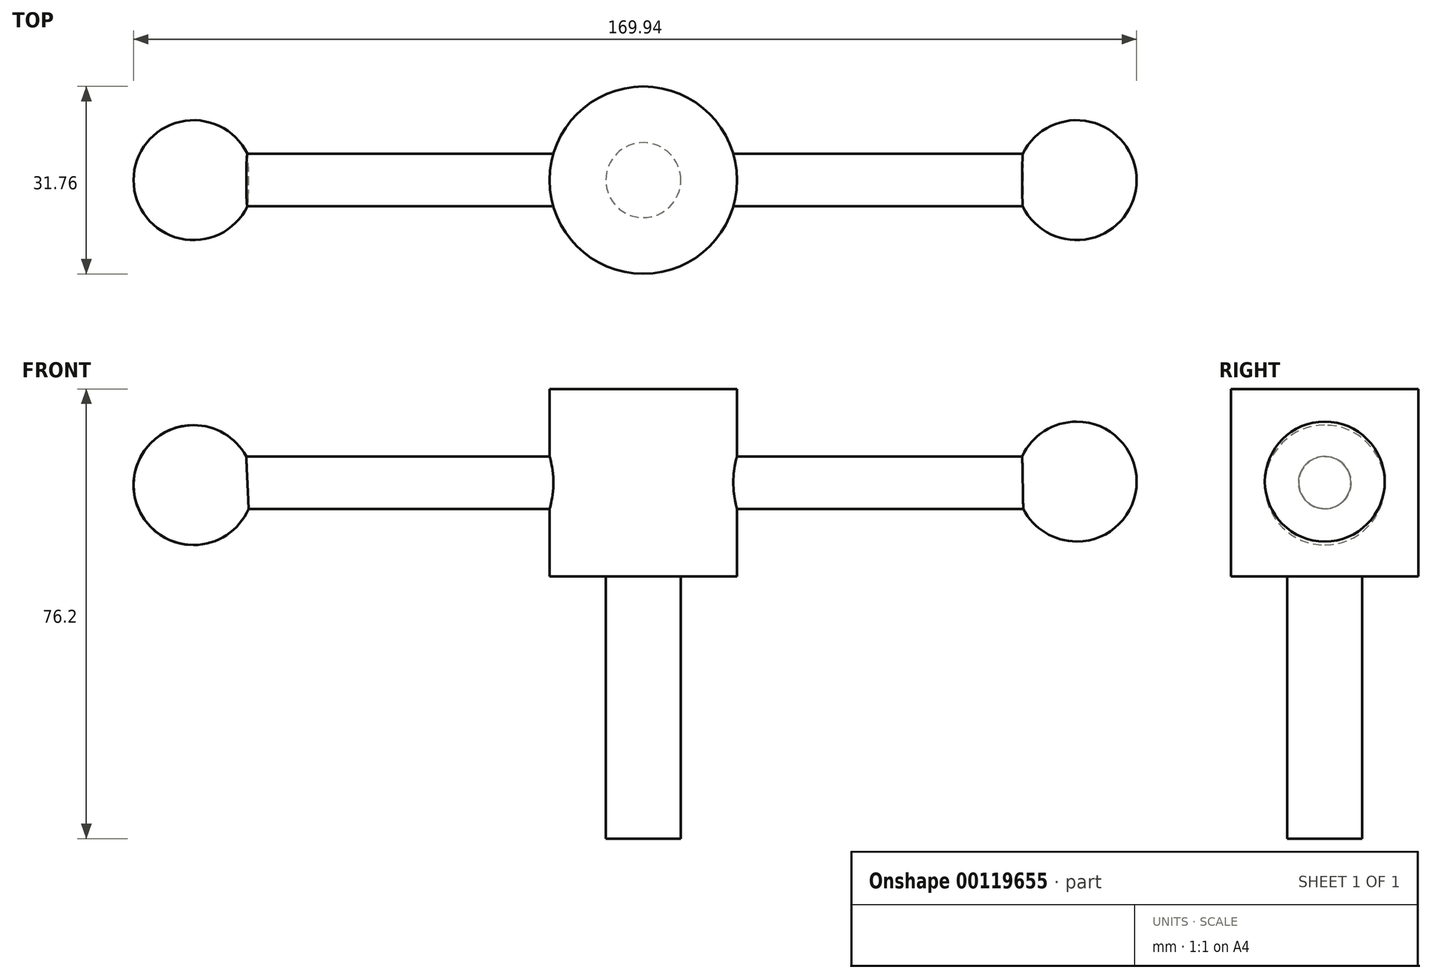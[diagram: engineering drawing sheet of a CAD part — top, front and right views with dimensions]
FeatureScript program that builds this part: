
annotation { "Feature Type Name" : "Feature", "Feature Type Description" : "" }
export const myFeature = defineFeature(function(context is Context, id is Id, definition is map)
    precondition{}
    {
        {
            var Q0;
            Q0=qCreatedBy(makeId("Top.planeOp"),FACE);
            var sketch = newSketch(context, id + "F0", { "sketchPlane" : qUnion([Q0])});
            skCircle(sketch, "E0", {"center": v(0, 0) * mm, "radius": 15.88 * mm});
            skCircle(sketch, "E1", {"center": v(0, 0) * mm, "radius": 6.35 * mm});
            skLineSegment(sketch, "E2", {"start": v(0, 0) * mm, "end": v(-109.61, 0) * mm, "construction": true});
            skSolve(sketch);
        }
        {
            var Q0;
            Q0=makeQuery(id+"F0.imprint","IMPRINT",FACE,{"disambiguationData":[TD([[makeQuery(id+"F0.imprint","IMPRINT",EDGE,{"derivedFrom":sQuery(id+"F0.wireOp",EDGE,"E0")}),1.0]])]});
            extrude(context, id + "F1", {"entities" : qUnion([Q0]), "oppositeDirection" : true, "depth" : 31.75 * mm});
        }
        {
            var Q0;
            Q0=makeQuery(id+"F0.imprint","IMPRINT",FACE,{"disambiguationData":[TD([[makeQuery(id+"F0.imprint","IMPRINT",EDGE,{"derivedFrom":sQuery(id+"F0.wireOp",EDGE,"E1")}),1.0]])]});
            extrude(context, id + "F2", {"entities" : qUnion([Q0]), "operationType" : NewBodyOperationType.ADD, "oppositeDirection" : true, "depth" : 76.2 * mm});
        }
        {
            var Q0;
            Q0=qCreatedBy(makeId("Right.planeOp"),FACE);
            var sketch = newSketch(context, id + "F3", { "sketchPlane" : qUnion([Q0])});
            skCircle(sketch, "E3", {"center": v(0, -15.88) * mm, "radius": 4.45 * mm});
            skSolve(sketch);
        }
        {
            var Q0;
            Q0 = qSketchRegion(id + "F3", true);
            extrude(context, id + "F4", {"entities" : qUnion([Q0]), "operationType" : NewBodyOperationType.ADD, "endBound" : BoundingType.SYMMETRIC, "depth" : 152.4 * mm});
        }
        {
            var Q0;
            Q0=qCreatedBy(makeId("Front.planeOp"),FACE);
            var sketch = newSketch(context, id + "F5", { "sketchPlane" : qUnion([Q0])});
            skArc(sketch, "E4", {"start": v(-76.2, -6.13) * mm, "mid": v(-86.36, -16.3) * mm, "end": v(-76.2, -26.45) * mm});
            skLineSegment(sketch, "E5", {"start": v(-76.2, -26.45) * mm, "end": v(-76.2, -6.13) * mm});
            skLineSegment(sketch, "E6", {"start": v(-76.2, -6.13) * mm, "end": v(-76.2, -58.23) * mm, "construction": true});
            skSolve(sketch);
        }
        {
            var Q0;
            Q0=makeQuery(id+"F5.imprint","IMPRINT",FACE,{"disambiguationData":[TD([[makeQuery(id+"F5.imprint","IMPRINT",EDGE,{"derivedFrom":sQuery(id+"F5.wireOp",EDGE,"E4")}),1.0]])]});
            var Q1;
            Q1=sQuery(id+"F5.wireOp",EDGE,"E6");
            revolve(context, id + "F6", {"entities" : qUnion([Q0]), "axis" : qUnion([Q1]), "revolveType" : RevolveType.FULL});
        }
        {
            var Q0;
            Q0=qCreatedBy(makeId("Front.planeOp"),FACE);
            var sketch = newSketch(context, id + "F7", { "sketchPlane" : qUnion([Q0])});
            skArc(sketch, "E7", {"start": v(73.42, -25.86) * mm, "mid": v(83.58, -15.7) * mm, "end": v(73.42, -5.54) * mm});
            skLineSegment(sketch, "E8", {"start": v(73.42, -5.54) * mm, "end": v(73.42, -46.73) * mm, "construction": true});
            skLineSegment(sketch, "E9", {"start": v(73.42, -5.54) * mm, "end": v(73.42, -25.86) * mm});
            skSolve(sketch);
        }
        {
            var Q0;
            Q0 = qSketchRegion(id + "F7", true);
            var Q1;
            Q1=sQuery(id+"F7.wireOp",EDGE,"E8");
            revolve(context, id + "F8", {"operationType" : NewBodyOperationType.ADD, "entities" : qUnion([Q0]), "axis" : qUnion([Q1]), "revolveType" : RevolveType.FULL});
        }
        {
            var Q0;
            Q0 = qSketchRegion(id + "F5", true);
            var Q1;
            Q1=sQuery(id+"F5.wireOp",EDGE,"E6");
            revolve(context, id + "F9", {"operationType" : NewBodyOperationType.ADD, "entities" : qUnion([Q0]), "axis" : qUnion([Q1]), "revolveType" : RevolveType.FULL});
        }
    });
